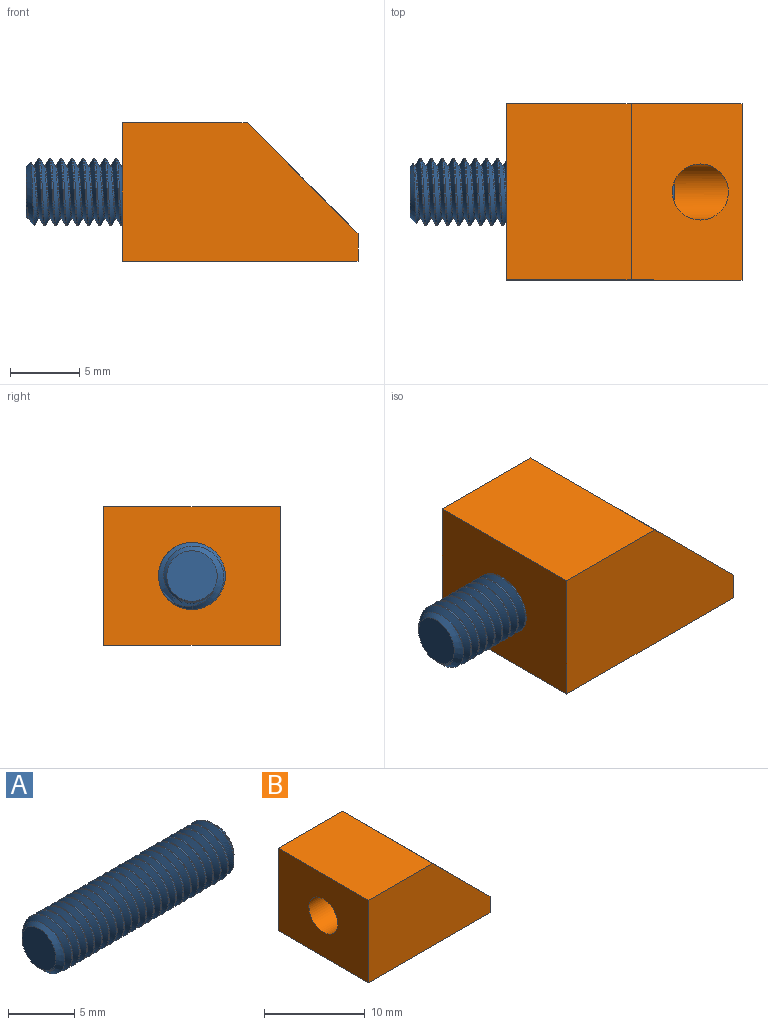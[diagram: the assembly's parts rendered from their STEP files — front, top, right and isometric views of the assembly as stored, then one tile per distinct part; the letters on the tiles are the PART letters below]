
ASSEMBLY  parts=2 mates=1
PART A: 9 faces, bbox 19.6x4.9x4.9 mm
  f0: cone r=1.82mm half-angle=45deg, axis (-1,0,0), area 6.1mm2, adj f3,f5,f6,f7,f8
  f1: cone r=2.41mm half-angle=45deg, axis (1,0,0), area 5.8mm2, adj f2,f4,f6,f7,f8
  f2: cone r=2.41mm half-angle=45deg, axis (1,0,0), area 0.3mm2, adj f1,f3,f6
  f3: cylinder r=2.41mm len=17.86mm, axis (1,0,0), area 33.8mm2, adj f0,f2,f6,f8
  f4: plane 3.64x3.64mm, normal (-1,0,0), area 10.4mm2, adj f1
  f5: plane 3.64x3.64mm, normal (1,0,0), area 10.4mm2, adj f0
  f6: bspline ~19.19x4.82mm, area 187mm2, adj f0,f1,f2,f3,f7
  f7: cylinder r=1.9mm len=18.89mm, axis (1,0,0), area 28.3mm2, adj f0,f1,f6,f8
  f8: bspline ~19.37x4.91mm, area 187.1mm2, adj f0,f1,f3,f7
PART B: 8 faces, bbox 17x12.7x10 mm
  f0: plane 12.7x10mm, normal (-1,0,0), area 114.2mm2, adj f1,f4,f5,f6,f7
  f1: plane 17x12.7mm, normal (0,0,-1), area 215.9mm2, adj f0,f2,f5,f6
  f2: plane 12.7x2mm, normal (1,0,0), area 25.4mm2, adj f1,f3,f5,f6
  f3: plane 12.7x8mm, normal (0.71,0,0.71), area 125.6mm2, adj f2,f4,f5,f6,f7
  f4: plane 12.7x9mm, normal (0,0,1), area 114.3mm2, adj f0,f3,f5,f6
  f5: plane 17x10mm, normal (0,-1,0), area 138mm2, adj f0,f1,f2,f3,f4
  f6: plane 17x10mm, normal (0,1,0), area 138mm2, adj f0,f1,f2,f3,f4
  f7: cylinder r=2.02mm len=16.05mm, axis (-1,0,0), area 177.6mm2, adj f0,f3
PLACE A t=(-11.47,-4.95,-2.6)mm
PLACE B t=(-5.56,1.4,-2.6)mm
MATE fastened A.f0 <-> B.f7  axis (1,0,0) through (-1.95,-4.95,-2.6)mm
